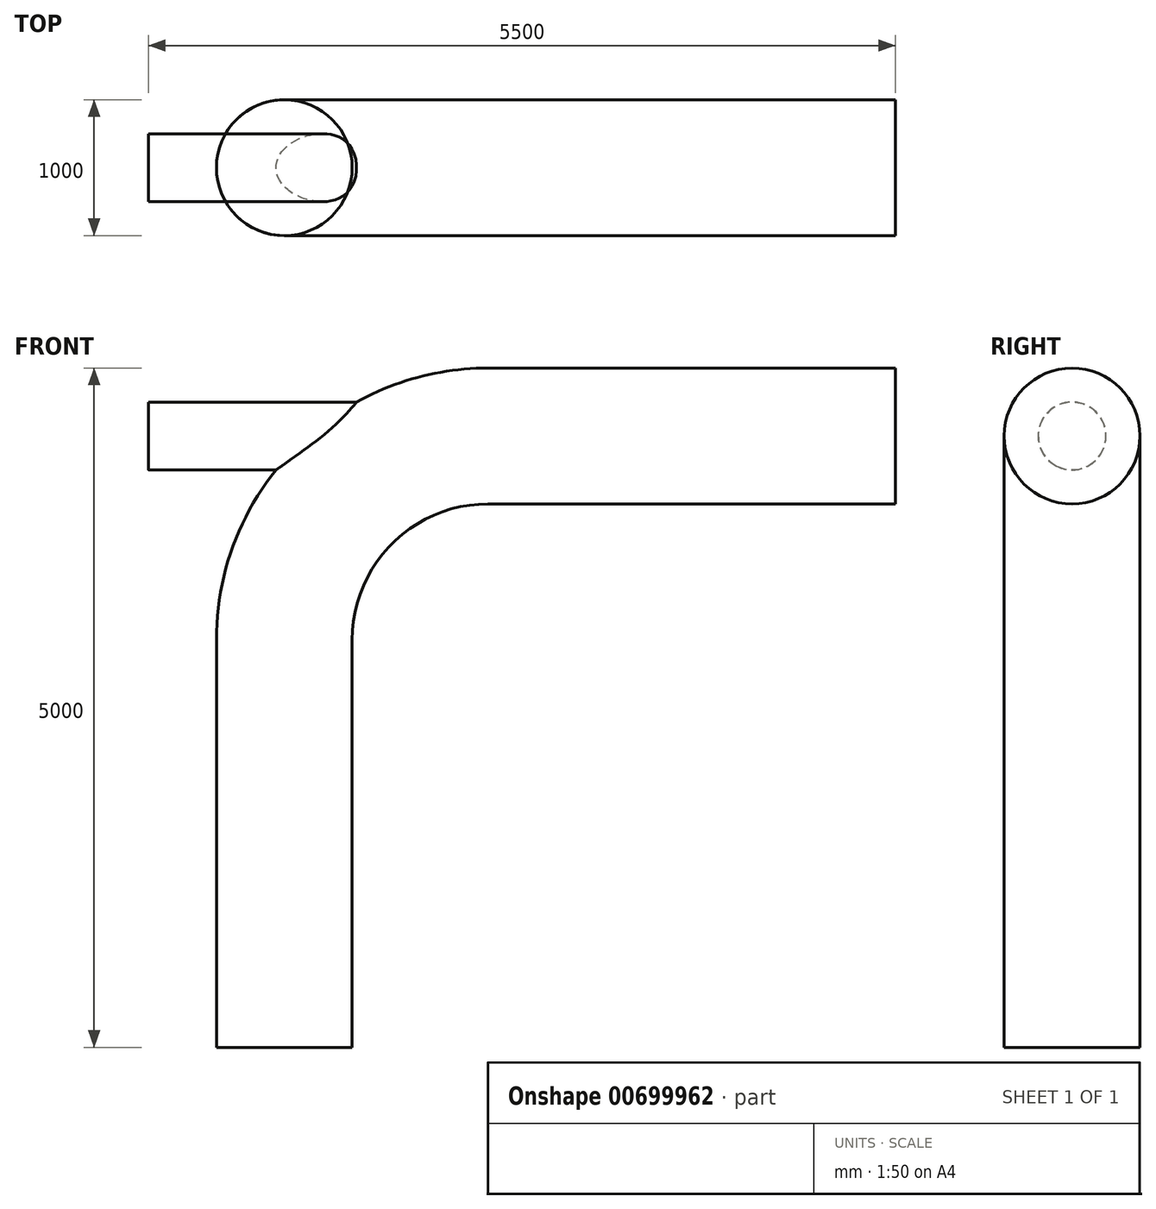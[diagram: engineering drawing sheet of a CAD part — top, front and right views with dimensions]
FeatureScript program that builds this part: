
annotation { "Feature Type Name" : "Feature", "Feature Type Description" : "" }
export const myFeature = defineFeature(function(context is Context, id is Id, definition is map)
    precondition{}
    {
        {
            var Q0;
            Q0=qCreatedBy(makeId("Front.planeOp"),FACE);
            var sketch = newSketch(context, id + "F0", { "sketchPlane" : qUnion([Q0])});
            skLineSegment(sketch, "E0", {"start": v(0, 0) * mm, "end": v(0, 3000) * mm});
            skArc(sketch, "E1", {"start": v(1500, 4500) * mm, "mid": v(439.34, 4060.66) * mm, "end": v(0, 3000) * mm});
            skLineSegment(sketch, "E2", {"start": v(1500, 4500) * mm, "end": v(4500, 4500) * mm});
            skSolve(sketch);
        }
        {
            var Q0;
            Q0=qCreatedBy(makeId("Top.planeOp"),FACE);
            var sketch = newSketch(context, id + "F1", { "sketchPlane" : qUnion([Q0])});
            skCircle(sketch, "E3", {"center": v(0, 0) * mm, "radius": 500 * mm});
            skSolve(sketch);
        }
        {
            var Q0;
            Q0=makeQuery(id+"F1.imprint","IMPRINT",FACE,{"disambiguationData":[TD([[makeQuery(id+"F1.imprint","IMPRINT",EDGE,{"derivedFrom":sQuery(id+"F1.wireOp",EDGE,"E3")}),1.0]])]});
            var Q1;
            Q1 = qConstructionFilter(qBodyType(qCreatedBy(id + "F0" ,EDGE), BodyType.WIRE), ConstructionObject.NO);
            sweep(context, id + "F2", {"profiles" : qUnion([Q0]), "path" : qUnion([Q1])});
        }
        {
            var Q0;
            Q0=qCreatedBy(makeId("Right.planeOp"),FACE);
            cPlane(context, id + "F3", {"entities" : qUnion([Q0]), "cplaneType" : CPlaneType.OFFSET, "offset" : 1000 * mm, "oppositeDirection" : true, "width" : 150 * mm, "height" : 150 * mm});
        }
        {
            var Q0;
            Q0=qCreatedBy(id+"F3.planeOp",FACE);
            var sketch = newSketch(context, id + "F4", { "sketchPlane" : qUnion([Q0])});
            skCircle(sketch, "E4", {"center": v(0, 4500) * mm, "radius": 250 * mm});
            skSolve(sketch);
        }
        {
            var Q0;
            Q0 = qSketchRegion(id + "F4", true);
            extrude(context, id + "F5", {"entities" : qUnion([Q0]), "operationType" : NewBodyOperationType.ADD, "depth" : 3000 * mm, "offsetDistance" : 25 * mm});
        }
    });
